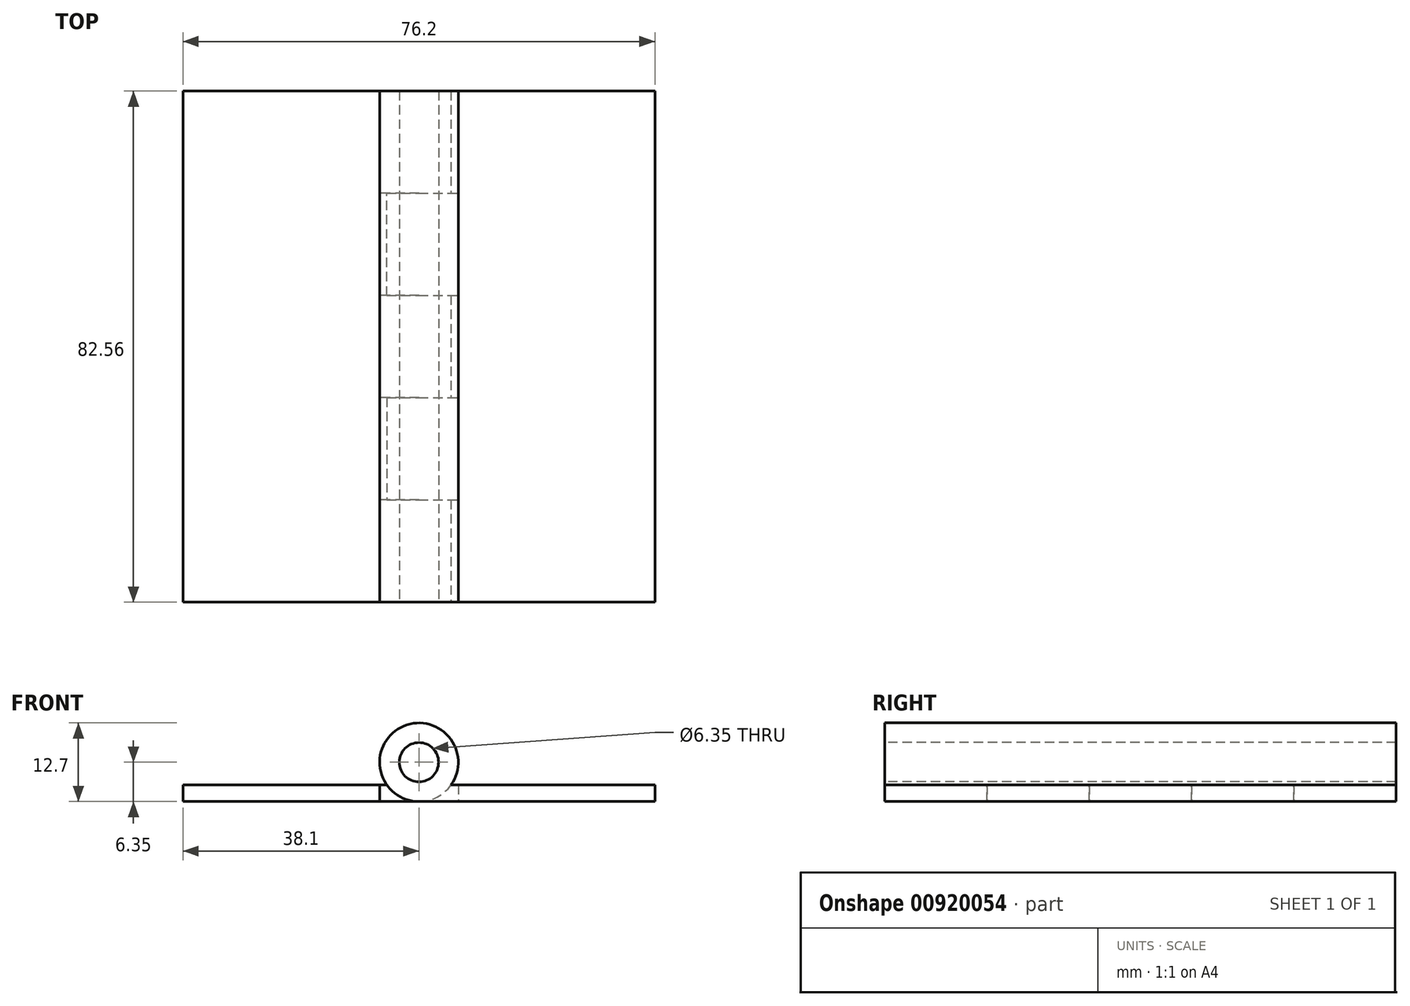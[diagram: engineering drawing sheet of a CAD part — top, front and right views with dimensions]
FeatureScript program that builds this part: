
annotation { "Feature Type Name" : "Feature", "Feature Type Description" : "" }
export const myFeature = defineFeature(function(context is Context, id is Id, definition is map)
    precondition{}
    {
        {
            var Q0;
            Q0=qCreatedBy(makeId("Top.planeOp"),FACE);
            var sketch = newSketch(context, id + "F0", { "sketchPlane" : qUnion([Q0])});
            skLineSegment(sketch, "E0.bottom", {"start": v(0, 41.28) * mm, "end": v(31.75, 41.28) * mm});
            skLineSegment(sketch, "E0.top", {"start": v(0, -41.28) * mm, "end": v(31.75, -41.28) * mm});
            skLineSegment(sketch, "E0.left", {"start": v(0, 41.28) * mm, "end": v(0, -41.28) * mm});
            skLineSegment(sketch, "E0.right", {"start": v(31.75, 41.28) * mm, "end": v(31.75, -41.28) * mm});
            skSolve(sketch);
        }
        {
            var Q0;
            Q0=makeQuery(id+"F0.imprint","IMPRINT",FACE,{"disambiguationData":[TD([[makeQuery(id+"F0.imprint","IMPRINT",EDGE,{"derivedFrom":sQuery(id+"F0.wireOp",EDGE,"E0.bottom")}),-1.0]])]});
            extrude(context, id + "F1", {"entities" : qUnion([Q0]), "depth" : 2.67 * mm, "offsetDistance" : 25.4 * mm});
        }
        {
            var Q0;
            Q0=makeQuery(id+"F1.opExtrude","SWEPT_FACE",FACE,{"disambiguationData":[OSD([sQuery(id+"F0.wireOp",EDGE,"E0.left")])]});
            var sketch = newSketch(context, id + "F2", { "sketchPlane" : qUnion([Q0])});
            skLineSegment(sketch, "E1.0.0", {"start": v(-41.28, 0) * mm, "end": v(41.28, 0) * mm});
            skLineSegment(sketch, "E1.0.1", {"start": v(41.28, 0) * mm, "end": v(41.28, 2.67) * mm});
            skLineSegment(sketch, "E1.0.2", {"start": v(41.28, 2.67) * mm, "end": v(-41.28, 2.67) * mm});
            skLineSegment(sketch, "E1.0.3", {"start": v(-41.28, 2.67) * mm, "end": v(-41.28, 0) * mm});
            skLineSegment(sketch, "E2", {"start": v(-24.76, 2.67) * mm, "end": v(-24.76, 0) * mm});
            skLineSegment(sketch, "E3", {"start": v(-8.25, 2.67) * mm, "end": v(-8.25, 0) * mm});
            skLineSegment(sketch, "E4", {"start": v(8.26, 2.67) * mm, "end": v(8.26, 0) * mm});
            skLineSegment(sketch, "E5", {"start": v(24.77, 2.67) * mm, "end": v(24.77, 0) * mm});
            skLineSegment(sketch, "E6", {"start": v(-41.28, 1.33) * mm, "end": v(-24.76, 1.33) * mm, "construction": true});
            skLineSegment(sketch, "E7", {"start": v(-24.76, 1.33) * mm, "end": v(-8.25, 1.33) * mm, "construction": true});
            skLineSegment(sketch, "E8", {"start": v(-8.25, 1.33) * mm, "end": v(8.26, 1.33) * mm, "construction": true});
            skLineSegment(sketch, "E9", {"start": v(8.26, 1.33) * mm, "end": v(24.77, 1.33) * mm, "construction": true});
            skLineSegment(sketch, "E10", {"start": v(24.77, 1.33) * mm, "end": v(41.28, 1.33) * mm, "construction": true});
            skSolve(sketch);
        }
        {
            var Q0;
            {var subQ0=sQuery(id+"F2.wireOp",EDGE,"E1.0.3");Q0=makeQuery(id+"F2.imprint","IMPRINT",FACE,{"disambiguationData":[TD([[makeQuery(id+"F2.imprint","IMPRINT",EDGE,{"derivedFrom":subQ0}),1.0]])]});}
            var Q1;
            {var subQ0=sQuery(id+"F2.wireOp",EDGE,"E3");Q1=makeQuery(id+"F2.imprint","IMPRINT",FACE,{"disambiguationData":[TD([[makeQuery(id+"F2.imprint","IMPRINT",EDGE,{"derivedFrom":subQ0}),1.0]])]});}
            var Q2;
            {var subQ0=sQuery(id+"F2.wireOp",EDGE,"E1.0.1");Q2=makeQuery(id+"F2.imprint","IMPRINT",FACE,{"disambiguationData":[TD([[makeQuery(id+"F2.imprint","IMPRINT",EDGE,{"derivedFrom":subQ0}),-1.0]])]});}
            extrude(context, id + "F3", {"entities" : qUnion([Q0, Q1, Q2]), "operationType" : NewBodyOperationType.ADD, "depth" : 6.35 * mm, "offsetDistance" : 25.4 * mm});
        }
        {
            var Q0;
            Q0=makeQuery(id+"F3.boolean.opBoolean","MERGE",FACE,{"derivedFrom":[makeQuery(id+"F1.opExtrude","SWEPT_FACE",FACE,{"disambiguationData":[OSD([sQuery(id+"F0.wireOp",EDGE,"E0.top")])]}),makeQuery(id+"F3.opExtrude","SWEPT_FACE",FACE,{"disambiguationData":[OSD([sQuery(id+"F2.wireOp",EDGE,"E1.0.1")])]})]});
            var sketch = newSketch(context, id + "F4", { "sketchPlane" : qUnion([Q0])});
            skCircle(sketch, "E11", {"center": v(-6.35, 6.35) * mm, "radius": 6.35 * mm});
            skCircle(sketch, "E12", {"center": v(-6.35, 6.35) * mm, "radius": 3.18 * mm});
            skSolve(sketch);
        }
        {
            var Q0;
            Q0=makeQuery(id+"F4.imprint","IMPRINT",FACE,{"disambiguationData":[TD([[makeQuery(id+"F4.imprint","IMPRINT",EDGE,{"derivedFrom":sQuery(id+"F4.wireOp",EDGE,"E12")}),-1.0]])]});
            var Q1;
            Q1=makeQuery(id+"F3.opExtrude","SWEPT_FACE",FACE,{"disambiguationData":[OSD([sQuery(id+"F2.wireOp",EDGE,"E5")])]});
            extrude(context, id + "F5", {"entities" : qUnion([Q0]), "operationType" : NewBodyOperationType.ADD, "endBound" : BoundingType.UP_TO_SURFACE, "oppositeDirection" : true, "depth" : 25.4 * mm, "endBoundEntityFace" : qUnion([Q1]), "offsetDistance" : 25.4 * mm});
        }
        {
            var Q0;
            Q0=makeQuery(id+"F3.opExtrude","SWEPT_FACE",FACE,{"disambiguationData":[OSD([sQuery(id+"F2.wireOp",EDGE,"E4")])]});
            var sketch = newSketch(context, id + "F6", { "sketchPlane" : qUnion([Q0])});
            skCircle(sketch, "E13.0", {"center": v(-6.35, 6.35) * mm, "radius": 3.18 * mm});
            skCircle(sketch, "E14", {"center": v(-6.35, 6.35) * mm, "radius": 6.35 * mm});
            skSolve(sketch);
        }
        {
            var Q0;
            Q0=makeQuery(id+"F6.imprint","IMPRINT",FACE,{"disambiguationData":[TD([[makeQuery(id+"F6.imprint","IMPRINT",EDGE,{"derivedFrom":sQuery(id+"F6.wireOp",EDGE,"E13.0")}),-1.0]])]});
            var Q1;
            Q1=makeQuery(id+"F3.opExtrude","SWEPT_FACE",FACE,{"disambiguationData":[OSD([sQuery(id+"F2.wireOp",EDGE,"E3")])]});
            extrude(context, id + "F7", {"entities" : qUnion([Q0]), "operationType" : NewBodyOperationType.ADD, "endBound" : BoundingType.UP_TO_SURFACE, "oppositeDirection" : true, "depth" : 25.4 * mm, "endBoundEntityFace" : qUnion([Q1]), "offsetDistance" : 25.4 * mm});
        }
        {
            var Q0;
            Q0=makeQuery(id+"F3.opExtrude","SWEPT_FACE",FACE,{"disambiguationData":[OSD([sQuery(id+"F2.wireOp",EDGE,"E2")])]});
            var sketch = newSketch(context, id + "F8", { "sketchPlane" : qUnion([Q0])});
            skCircle(sketch, "E15.0", {"center": v(-6.35, 6.35) * mm, "radius": 3.18 * mm});
            skCircle(sketch, "E16", {"center": v(-6.35, 6.35) * mm, "radius": 6.35 * mm});
            skSolve(sketch);
        }
        {
            var Q0;
            Q0=makeQuery(id+"F8.imprint","IMPRINT",FACE,{"disambiguationData":[TD([[makeQuery(id+"F8.imprint","IMPRINT",EDGE,{"derivedFrom":sQuery(id+"F8.wireOp",EDGE,"E15.0")}),-1.0]])]});
            var Q1;
            Q1=makeQuery(id+"F3.boolean.opBoolean","MERGE",FACE,{"derivedFrom":[makeQuery(id+"F1.opExtrude","SWEPT_FACE",FACE,{"disambiguationData":[OSD([sQuery(id+"F0.wireOp",EDGE,"E0.bottom")])]}),makeQuery(id+"F3.opExtrude","SWEPT_FACE",FACE,{"disambiguationData":[OSD([sQuery(id+"F2.wireOp",EDGE,"E1.0.3")])]})]});
            extrude(context, id + "F9", {"entities" : qUnion([Q0]), "operationType" : NewBodyOperationType.ADD, "endBound" : BoundingType.UP_TO_SURFACE, "oppositeDirection" : true, "depth" : 25.4 * mm, "endBoundEntityFace" : qUnion([Q1]), "offsetDistance" : 25.4 * mm});
        }
        {
            var Q0;
            Q0=qCreatedBy(makeId("Top.planeOp"),FACE);
            var sketch = newSketch(context, id + "F10", { "sketchPlane" : qUnion([Q0])});
            skLineSegment(sketch, "E17", {"start": v(-12.7, 40) * mm, "end": v(-12.7, 41.28) * mm});
            skLineSegment(sketch, "E18", {"start": v(-12.7, -41.28) * mm, "end": v(-12.7, -40) * mm});
            skLineSegment(sketch, "E19.bottom", {"start": v(-44.45, 41.27) * mm, "end": v(-12.7, 41.27) * mm});
            skLineSegment(sketch, "E19.top", {"start": v(-44.45, -41.28) * mm, "end": v(-12.7, -41.28) * mm});
            skLineSegment(sketch, "E19.left", {"start": v(-44.45, 41.27) * mm, "end": v(-44.45, -41.28) * mm});
            skLineSegment(sketch, "E19.right", {"start": v(-12.7, 41.28) * mm, "end": v(-12.7, -41.28) * mm});
            skLineSegment(sketch, "E20", {"start": v(0, 0) * mm, "end": v(-12.7, 0) * mm, "construction": true});
            skSolve(sketch);
        }
        {
            var Q0;
            {var subQ0=sQuery(id+"F10.wireOp",EDGE,"E19.bottom");Q0=makeQuery(id+"F10.imprint","IMPRINT",FACE,{"disambiguationData":[TD([[makeQuery(id+"F10.imprint","IMPRINT",EDGE,{"derivedFrom":subQ0}),-1.0]])]});}
            extrude(context, id + "F11", {"entities" : qUnion([Q0]), "depth" : 2.67 * mm, "offsetDistance" : 25.4 * mm});
        }
        {
            var Q0;
            Q0=makeQuery(id+"F11.opExtrude","SWEPT_FACE",FACE,{"disambiguationData":[OSD([sQuery(id+"F10.wireOp",EDGE,"E19.right")])]});
            var sketch = newSketch(context, id + "F12", { "sketchPlane" : qUnion([Q0])});
            skLineSegment(sketch, "E21.0", {"start": v(-24.77, 2.67) * mm, "end": v(-24.77, 0) * mm});
            skLineSegment(sketch, "E22.0", {"start": v(-8.26, 2.67) * mm, "end": v(-8.26, 0) * mm});
            skLineSegment(sketch, "E23.0", {"start": v(8.25, 2.67) * mm, "end": v(8.25, 0) * mm});
            skLineSegment(sketch, "E24.0", {"start": v(24.76, 2.67) * mm, "end": v(24.76, 0) * mm});
            skLineSegment(sketch, "E25", {"start": v(-24.77, 2.67) * mm, "end": v(-8.26, 2.67) * mm});
            skLineSegment(sketch, "E26", {"start": v(-8.26, 0) * mm, "end": v(-24.77, 0) * mm});
            skLineSegment(sketch, "E27", {"start": v(8.25, 2.67) * mm, "end": v(24.76, 2.67) * mm});
            skLineSegment(sketch, "E28", {"start": v(24.76, 0) * mm, "end": v(8.25, 0) * mm});
            skSolve(sketch);
        }
        {
            var Q0;
            Q0=makeQuery(id+"F12.imprint","IMPRINT",FACE,{"disambiguationData":[TD([[makeQuery(id+"F12.imprint","IMPRINT",EDGE,{"derivedFrom":sQuery(id+"F12.wireOp",EDGE,"E21.0")}),1.0]])]});
            var Q1;
            Q1=makeQuery(id+"F12.imprint","IMPRINT",FACE,{"disambiguationData":[TD([[makeQuery(id+"F12.imprint","IMPRINT",EDGE,{"derivedFrom":sQuery(id+"F12.wireOp",EDGE,"E23.0")}),1.0]])]});
            extrude(context, id + "F13", {"entities" : qUnion([Q0, Q1]), "operationType" : NewBodyOperationType.ADD, "depth" : 6.35 * mm, "offsetDistance" : 25.4 * mm});
        }
        {
            var Q0;
            {var subQ0=sQuery(id+"F2.wireOp",EDGE,"E2");Q0=makeQuery(id+"F9.boolean.opBoolean","MERGE",FACE,{"derivedFrom":[makeQuery(id+"F3.opExtrude","SWEPT_FACE",FACE,{"disambiguationData":[OSD([subQ0])]}),makeQuery(id+"F9.opExtrude","CAP_FACE",FACE,{"disambiguationData":[OSD([sQuery(id+"F2.wireOp",EDGE,"E1.0.2"),subQ0,sQuery(id+"F8.wireOp",EDGE,"E15.0"),sQuery(id+"F8.wireOp",EDGE,"E16")])],"isStart":true})]});}
            var sketch = newSketch(context, id + "F14", { "sketchPlane" : qUnion([Q0])});
            skCircle(sketch, "E29.0", {"center": v(-6.35, 6.35) * mm, "radius": 3.18 * mm});
            skCircle(sketch, "E30", {"center": v(-6.35, 6.35) * mm, "radius": 6.35 * mm});
            skSolve(sketch);
        }
        {
            var Q0;
            Q0=makeQuery(id+"F14.imprint","IMPRINT",FACE,{"disambiguationData":[TD([[makeQuery(id+"F14.imprint","IMPRINT",EDGE,{"derivedFrom":sQuery(id+"F14.wireOp",EDGE,"E29.0")}),-1.0]])]});
            extrude(context, id + "F15", {"entities" : qUnion([Q0]), "operationType" : NewBodyOperationType.ADD, "endBound" : BoundingType.UP_TO_NEXT, "depth" : 25.4 * mm, "offsetDistance" : 25.4 * mm});
        }
        {
            var Q0;
            Q0=makeQuery(id+"F5.boolean.opBoolean","MERGE",FACE,{"derivedFrom":[makeQuery(id+"F3.opExtrude","SWEPT_FACE",FACE,{"disambiguationData":[OSD([sQuery(id+"F2.wireOp",EDGE,"E5")])]}),makeQuery(id+"F5.opExtrude","CAP_FACE",FACE,{"disambiguationData":[OSD([sQuery(id+"F0.wireOp",EDGE,"E0.top"),sQuery(id+"F2.wireOp",EDGE,"E1.0.1"),sQuery(id+"F2.wireOp",EDGE,"E1.0.2"),sQuery(id+"F4.wireOp",EDGE,"E11"),sQuery(id+"F4.wireOp",EDGE,"E12")])],"isStart":false})]});
            var sketch = newSketch(context, id + "F16", { "sketchPlane" : qUnion([Q0])});
            skCircle(sketch, "E31.0", {"center": v(6.35, 6.35) * mm, "radius": 3.18 * mm});
            skCircle(sketch, "E32", {"center": v(6.35, 6.35) * mm, "radius": 6.35 * mm});
            skSolve(sketch);
        }
        {
            var Q0;
            Q0=makeQuery(id+"F16.imprint","IMPRINT",FACE,{"disambiguationData":[TD([[makeQuery(id+"F16.imprint","IMPRINT",EDGE,{"derivedFrom":sQuery(id+"F16.wireOp",EDGE,"E31.0")}),-1.0]])]});
            extrude(context, id + "F17", {"entities" : qUnion([Q0]), "operationType" : NewBodyOperationType.ADD, "endBound" : BoundingType.UP_TO_NEXT, "depth" : 25.4 * mm, "offsetDistance" : 25.4 * mm});
        }
    });
